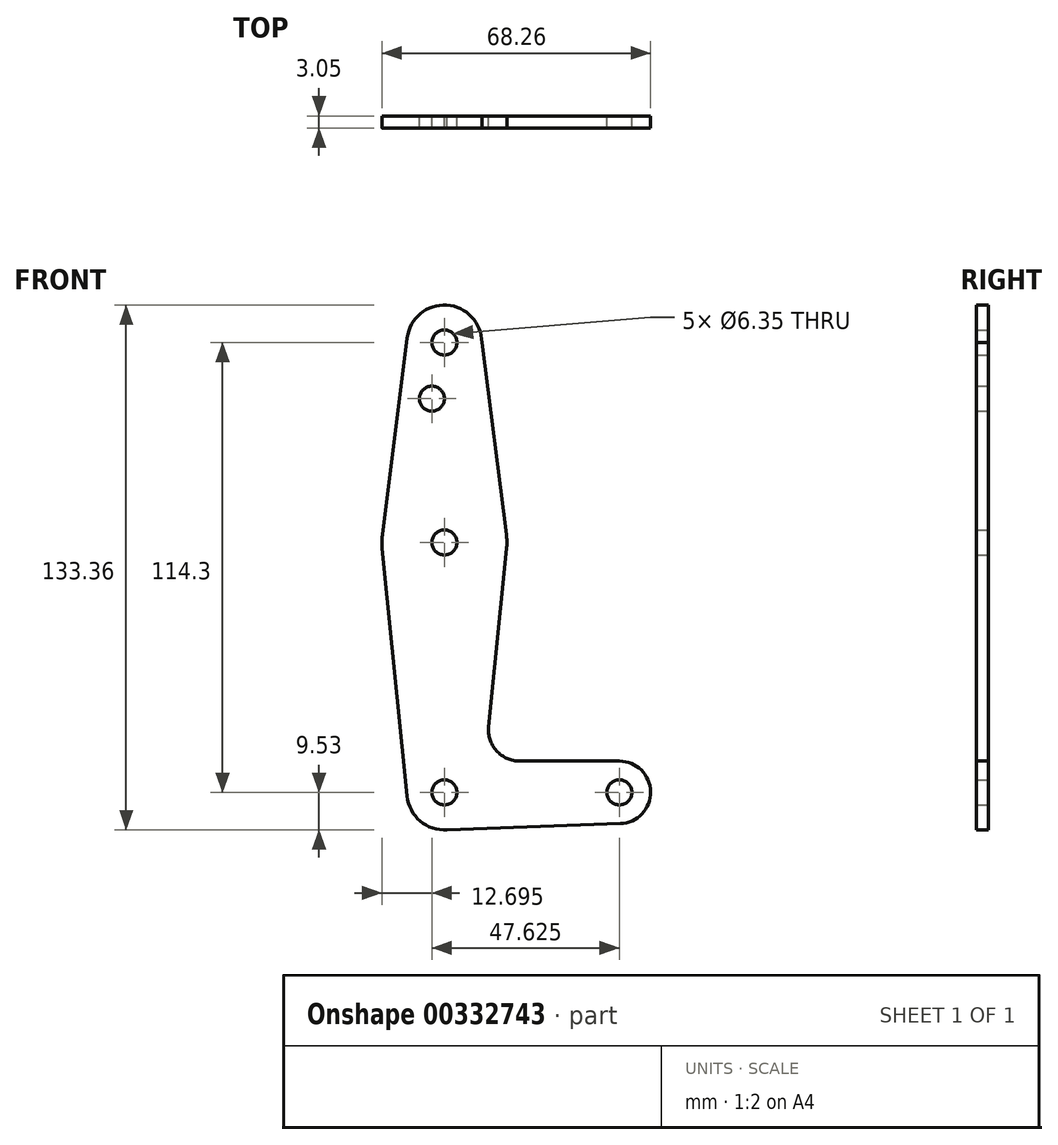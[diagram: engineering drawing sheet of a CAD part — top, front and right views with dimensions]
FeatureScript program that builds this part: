
annotation { "Feature Type Name" : "Feature", "Feature Type Description" : "" }
export const myFeature = defineFeature(function(context is Context, id is Id, definition is map)
    precondition{}
    {
        {
            var Q0;
            Q0=qCreatedBy(makeId("Front.planeOp"),FACE);
            var sketch = newSketch(context, id + "F0", { "sketchPlane" : qUnion([Q0])});
            skLineSegment(sketch, "E0", {"start": v(0, 114.3) * mm, "end": v(0, 0) * mm, "construction": true});
            skLineSegment(sketch, "E1", {"start": v(0, 0) * mm, "end": v(44.45, 0) * mm, "construction": true});
            skCircle(sketch, "E2", {"center": v(0, 114.3) * mm, "radius": 9.53 * mm});
            skCircle(sketch, "E3", {"center": v(44.45, 0) * mm, "radius": 7.94 * mm});
            skCircle(sketch, "E4", {"center": v(0, 0) * mm, "radius": 9.53 * mm});
            skCircle(sketch, "E5", {"center": v(0, 63.5) * mm, "radius": 15.88 * mm});
            skLineSegment(sketch, "E6", {"start": v(-15.8, 61.91) * mm, "end": v(-9.48, -0.95) * mm});
            skLineSegment(sketch, "E7", {"start": v(15.8, 61.91) * mm, "end": v(11.25, 16.68) * mm});
            skLineSegment(sketch, "E8", {"start": v(-9.45, 115.5) * mm, "end": v(-15.75, 65.48) * mm});
            skLineSegment(sketch, "E9", {"start": v(9.52, 114.3) * mm, "end": v(15.75, 65.48) * mm});
            skLineSegment(sketch, "E10", {"start": v(19.16, 7.94) * mm, "end": v(44.45, 7.94) * mm});
            skLineSegment(sketch, "E11", {"start": v(0, -9.53) * mm, "end": v(44.73, -7.93) * mm});
            skPoint(sketch, "E12.newPointA", {"position": v(9.48, -0.95) * mm});
            skArc(sketch, "E12.filletArc", {"start": v(11.25, 16.68) * mm, "mid": v(13.26, 10.55) * mm, "end": v(19.16, 7.94) * mm});
            skCircle(sketch, "E13", {"center": v(0, 114.3) * mm, "radius": 3.18 * mm});
            skCircle(sketch, "E14", {"center": v(0, 63.5) * mm, "radius": 3.18 * mm});
            skCircle(sketch, "E15", {"center": v(0, 0) * mm, "radius": 3.18 * mm});
            skCircle(sketch, "E16", {"center": v(44.45, 0) * mm, "radius": 3.18 * mm});
            skCircle(sketch, "E17", {"center": v(-3.17, 100.03) * mm, "radius": 3.18 * mm});
            skSolve(sketch);
        }
        {
            var Q0;
            Q0 = qSketchRegion(id + "F0", true);
            extrude(context, id + "F1", {"entities" : qUnion([Q0]), "depth" : 3.05 * mm});
        }
    });
